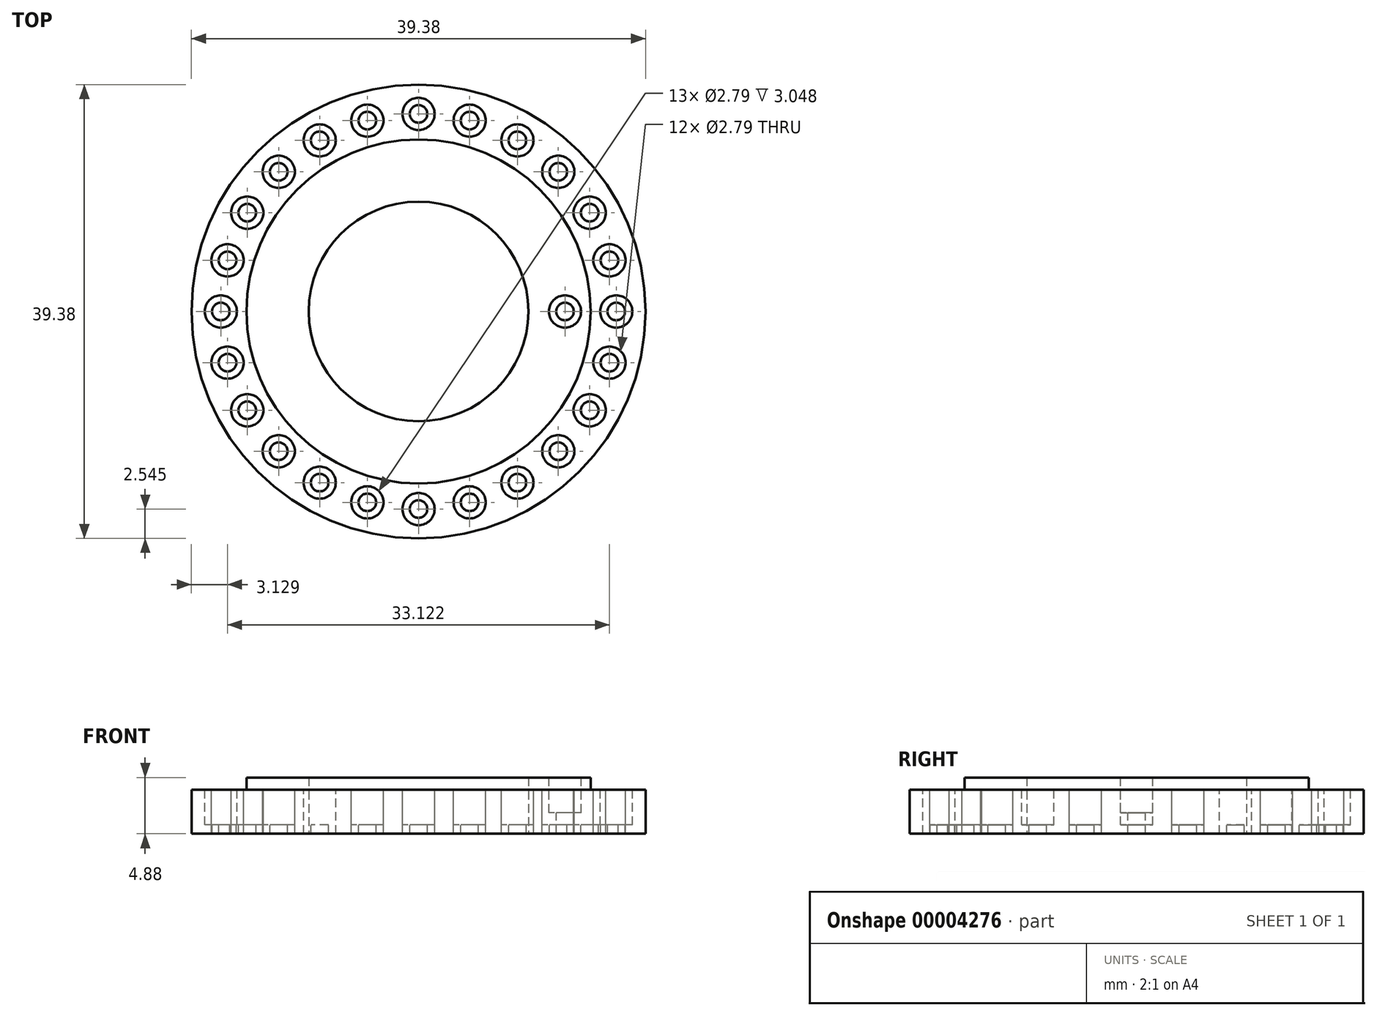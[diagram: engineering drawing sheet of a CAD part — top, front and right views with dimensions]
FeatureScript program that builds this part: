
annotation { "Feature Type Name" : "Feature", "Feature Type Description" : "" }
export const myFeature = defineFeature(function(context is Context, id is Id, definition is map)
    precondition{}
    {
        {
            var Q0;
            Q0=qCreatedBy(makeId("Top.planeOp"),FACE);
            var sketch = newSketch(context, id + "F0", { "sketchPlane" : qUnion([Q0])});
            skCircle(sketch, "E0", {"center": v(0, 0) * mm, "radius": 19.69 * mm});
            skCircle(sketch, "E1", {"center": v(0, 0) * mm, "radius": 14.92 * mm});
            skCircle(sketch, "E2", {"center": v(0, 0) * mm, "radius": 9.53 * mm});
            skSolve(sketch);
        }
        {
            var Q0;
            Q0=makeQuery(id+"F0.imprint","IMPRINT",FACE,{"disambiguationData":[TD([[makeQuery(id+"F0.imprint","IMPRINT",EDGE,{"derivedFrom":sQuery(id+"F0.wireOp",EDGE,"E1")}),1.0]])]});
            extrude(context, id + "F1", {"entities" : qUnion([Q0]), "flatOperationType" : FlatOperationType.REMOVE, "depth" : 4.88 * mm, "offsetDistance" : 25.4 * mm, "domain" : OperationDomain.MODEL});
        }
        {
            var Q0;
            Q0=makeQuery(id+"F0.imprint","IMPRINT",FACE,{"disambiguationData":[TD([[makeQuery(id+"F0.imprint","IMPRINT",EDGE,{"derivedFrom":sQuery(id+"F0.wireOp",EDGE,"E0")}),1.0]])]});
            extrude(context, id + "F2", {"entities" : qUnion([Q0]), "operationType" : NewBodyOperationType.ADD, "flatOperationType" : FlatOperationType.REMOVE, "depth" : 3.8 * mm, "offsetDistance" : 25.4 * mm, "domain" : OperationDomain.MODEL});
        }
        {
            var Q0;
            Q0=makeQuery(id+"F1.opExtrude","CAP_FACE",FACE,{"disambiguationData":[OSD([sQuery(id+"F0.wireOp",EDGE,"E1"),sQuery(id+"F0.wireOp",EDGE,"E2")])],"isStart":false});
            var sketch = newSketch(context, id + "F3", { "sketchPlane" : qUnion([Q0])});
            skLineSegment(sketch, "E3", {"start": v(0, 0) * mm, "end": v(11.3, 0) * mm});
            skCircle(sketch, "E4", {"center": v(12.7, 0) * mm, "radius": 0.76 * mm});
            skLineSegment(sketch, "E5.trimOffspring", {"start": v(14.1, 0) * mm, "end": v(14.92, 0) * mm});
            skCircle(sketch, "E6", {"center": v(12.7, 0) * mm, "radius": 1.4 * mm});
            skSolve(sketch);
        }
        {
            var Q0;
            {var subQ0=sQuery(id+"F3.wireOp",EDGE,"E4");var subQ2=makeQuery(id+"F3.imprint","INTERSECT",VERTEX,{"derivedFrom":[sQuery(id+"F3.wireOp",EDGE,"E3"),subQ0]});Q0=makeQuery(id+"F3.imprint","IMPRINT",FACE,{"disambiguationData":[TD([[makeQuery(id+"F3.imprint","IMPRINT",EDGE,{"disambiguationData":[TD([[subQ2,1.0]])],"derivedFrom":subQ0}),1.0]])]});}
            var Q1;
            Q1=qSketchRegion(id+"F5",true);
            extrude(context, id + "F4", {"entities" : qUnion([Q0, Q1]), "operationType" : NewBodyOperationType.REMOVE, "flatOperationType" : FlatOperationType.REMOVE, "endBound" : BoundingType.THROUGH_ALL, "oppositeDirection" : true, "depth" : 4.44 * mm, "offsetDistance" : 25.4 * mm, "domain" : OperationDomain.MODEL});
        }
        {
            var Q0;
            Q0=makeQuery(id+"F2.opExtrude","CAP_FACE",FACE,{"disambiguationData":[OSD([sQuery(id+"F0.wireOp",EDGE,"E0"),sQuery(id+"F0.wireOp",EDGE,"E1")])],"isStart":false});
            var sketch = newSketch(context, id + "F5", { "sketchPlane" : qUnion([Q0])});
            skLineSegment(sketch, "E7", {"start": v(0, 0) * mm, "end": v(16.38, 0) * mm, "construction": true});
            skLineSegment(sketch, "E8", {"start": v(0, 0) * mm, "end": v(15.82, 4.24) * mm, "construction": true});
            skCircle(sketch, "E9", {"center": v(17.15, 0) * mm, "radius": 0.76 * mm});
            skCircle(sketch, "E10", {"center": v(16.56, 4.44) * mm, "radius": 0.76 * mm});
            skCircle(sketch, "E11.0.MirrorC", {"center": v(14.85, 8.57) * mm, "radius": 0.76 * mm});
            skLineSegment(sketch, "E12", {"start": v(0, 0) * mm, "end": v(14.19, 8.2) * mm, "construction": true});
            skCircle(sketch, "E13.0.MirrorC", {"center": v(12.12, 12.12) * mm, "radius": 0.76 * mm});
            skCircle(sketch, "E14.0.MirrorC", {"center": v(8.57, 14.85) * mm, "radius": 0.76 * mm});
            skLineSegment(sketch, "E15", {"start": v(0, 0) * mm, "end": v(8.2, 14.19) * mm, "construction": true});
            skCircle(sketch, "E16.0.MirrorC", {"center": v(4.44, 16.56) * mm, "radius": 0.76 * mm});
            skCircle(sketch, "E17.0.MirrorC", {"center": v(0, 17.15) * mm, "radius": 0.76 * mm});
            skCircle(sketch, "E18.0.MirrorC", {"center": v(-4.44, 16.56) * mm, "radius": 0.76 * mm});
            skCircle(sketch, "E19.0.MirrorC", {"center": v(-8.57, 14.85) * mm, "radius": 0.76 * mm});
            skLineSegment(sketch, "E20", {"start": v(0, 0) * mm, "end": v(-8.2, 14.19) * mm, "construction": true});
            skCircle(sketch, "E21.0.MirrorC", {"center": v(-12.12, 12.12) * mm, "radius": 0.76 * mm});
            skCircle(sketch, "E22.0.MirrorC", {"center": v(-14.85, 8.57) * mm, "radius": 0.76 * mm});
            skCircle(sketch, "E23.0.MirrorC", {"center": v(-16.56, 4.44) * mm, "radius": 0.76 * mm});
            skCircle(sketch, "E24.0.MirrorC", {"center": v(-17.15, 0) * mm, "radius": 0.76 * mm});
            skCircle(sketch, "E25.0.MirrorC", {"center": v(-16.56, -4.44) * mm, "radius": 0.76 * mm});
            skCircle(sketch, "E26.0.MirrorC", {"center": v(-14.85, -8.57) * mm, "radius": 0.76 * mm});
            skCircle(sketch, "E27.0.MirrorC", {"center": v(-12.12, -12.12) * mm, "radius": 0.76 * mm});
            skCircle(sketch, "E28.0.MirrorC", {"center": v(-8.57, -14.85) * mm, "radius": 0.76 * mm});
            skCircle(sketch, "E29.0.MirrorC", {"center": v(16.56, -4.44) * mm, "radius": 0.76 * mm});
            skCircle(sketch, "E30.0.MirrorC", {"center": v(14.85, -8.57) * mm, "radius": 0.76 * mm});
            skCircle(sketch, "E31.0.MirrorC", {"center": v(12.12, -12.12) * mm, "radius": 0.76 * mm});
            skCircle(sketch, "E32.0.MirrorC", {"center": v(8.57, -14.85) * mm, "radius": 0.76 * mm});
            skCircle(sketch, "E33.0.MirrorC", {"center": v(4.44, -16.56) * mm, "radius": 0.76 * mm});
            skCircle(sketch, "E34.0.MirrorC", {"center": v(0, -17.15) * mm, "radius": 0.76 * mm});
            skCircle(sketch, "E35.0.MirrorC", {"center": v(-4.44, -16.56) * mm, "radius": 0.76 * mm});
            skLineSegment(sketch, "E36.trimOffspring", {"start": v(17.3, 4.63) * mm, "end": v(19.01, 5.1) * mm, "construction": true});
            skLineSegment(sketch, "E37.trimOffspring", {"start": v(17.9, 0) * mm, "end": v(19.69, 0) * mm, "construction": true});
            skCircle(sketch, "E38", {"center": v(17.15, 0) * mm, "radius": 1.4 * mm});
            skCircle(sketch, "E39", {"center": v(16.56, 4.44) * mm, "radius": 1.4 * mm});
            skCircle(sketch, "E40", {"center": v(14.85, 8.57) * mm, "radius": 1.4 * mm});
            skCircle(sketch, "E41", {"center": v(12.12, 12.12) * mm, "radius": 1.4 * mm});
            skCircle(sketch, "E42", {"center": v(8.57, 14.85) * mm, "radius": 1.4 * mm});
            skCircle(sketch, "E43", {"center": v(4.44, 16.56) * mm, "radius": 1.4 * mm});
            skCircle(sketch, "E44", {"center": v(0, 17.15) * mm, "radius": 1.4 * mm});
            skCircle(sketch, "E45", {"center": v(-4.44, 16.56) * mm, "radius": 1.4 * mm});
            skCircle(sketch, "E46", {"center": v(-8.57, 14.85) * mm, "radius": 1.4 * mm});
            skCircle(sketch, "E47", {"center": v(-12.12, 12.12) * mm, "radius": 1.4 * mm});
            skCircle(sketch, "E48", {"center": v(-14.85, 8.57) * mm, "radius": 1.4 * mm});
            skCircle(sketch, "E49", {"center": v(-16.56, 4.44) * mm, "radius": 1.4 * mm});
            skCircle(sketch, "E50", {"center": v(-17.15, 0) * mm, "radius": 1.4 * mm});
            skCircle(sketch, "E51", {"center": v(-16.56, -4.44) * mm, "radius": 1.4 * mm});
            skCircle(sketch, "E52", {"center": v(-14.85, -8.57) * mm, "radius": 1.4 * mm});
            skCircle(sketch, "E53", {"center": v(-12.12, -12.12) * mm, "radius": 1.4 * mm});
            skCircle(sketch, "E54", {"center": v(-8.57, -14.85) * mm, "radius": 1.4 * mm});
            skCircle(sketch, "E55", {"center": v(-4.44, -16.56) * mm, "radius": 1.4 * mm});
            skCircle(sketch, "E56", {"center": v(0, -17.15) * mm, "radius": 1.4 * mm});
            skCircle(sketch, "E57", {"center": v(4.44, -16.56) * mm, "radius": 1.4 * mm});
            skCircle(sketch, "E58", {"center": v(8.57, -14.85) * mm, "radius": 1.4 * mm});
            skCircle(sketch, "E59", {"center": v(12.12, -12.12) * mm, "radius": 1.4 * mm});
            skCircle(sketch, "E60", {"center": v(14.85, -8.57) * mm, "radius": 1.4 * mm});
            skCircle(sketch, "E61", {"center": v(16.56, -4.44) * mm, "radius": 1.4 * mm});
            skSolve(sketch);
        }
        {
            var Q0;
            Q0=makeQuery(id+"F5.imprint","IMPRINT",FACE,{"disambiguationData":[TD([[makeQuery(id+"F5.imprint","IMPRINT",EDGE,{"derivedFrom":sQuery(id+"F5.wireOp",EDGE,"E9")}),1.0]])]});
            var Q1;
            Q1=makeQuery(id+"F5.imprint","IMPRINT",FACE,{"disambiguationData":[TD([[makeQuery(id+"F5.imprint","IMPRINT",EDGE,{"derivedFrom":sQuery(id+"F5.wireOp",EDGE,"E10")}),1.0]])]});
            var Q2;
            Q2=makeQuery(id+"F5.imprint","IMPRINT",FACE,{"disambiguationData":[TD([[makeQuery(id+"F5.imprint","IMPRINT",EDGE,{"derivedFrom":sQuery(id+"F5.wireOp",EDGE,"E11.0.MirrorC")}),-1.0]])]});
            var Q3;
            Q3=makeQuery(id+"F5.imprint","IMPRINT",FACE,{"disambiguationData":[TD([[makeQuery(id+"F5.imprint","IMPRINT",EDGE,{"derivedFrom":sQuery(id+"F5.wireOp",EDGE,"E13.0.MirrorC")}),-1.0]])]});
            var Q4;
            Q4=makeQuery(id+"F5.imprint","IMPRINT",FACE,{"disambiguationData":[TD([[makeQuery(id+"F5.imprint","IMPRINT",EDGE,{"derivedFrom":sQuery(id+"F5.wireOp",EDGE,"E14.0.MirrorC")}),-1.0]])]});
            var Q5;
            Q5=makeQuery(id+"F5.imprint","IMPRINT",FACE,{"disambiguationData":[TD([[makeQuery(id+"F5.imprint","IMPRINT",EDGE,{"derivedFrom":sQuery(id+"F5.wireOp",EDGE,"E16.0.MirrorC")}),1.0]])]});
            var Q6;
            Q6=makeQuery(id+"F5.imprint","IMPRINT",FACE,{"disambiguationData":[TD([[makeQuery(id+"F5.imprint","IMPRINT",EDGE,{"derivedFrom":sQuery(id+"F5.wireOp",EDGE,"E17.0.MirrorC")}),1.0]])]});
            var Q7;
            Q7=makeQuery(id+"F5.imprint","IMPRINT",FACE,{"disambiguationData":[TD([[makeQuery(id+"F5.imprint","IMPRINT",EDGE,{"derivedFrom":sQuery(id+"F5.wireOp",EDGE,"E18.0.MirrorC")}),-1.0]])]});
            var Q8;
            Q8=makeQuery(id+"F5.imprint","IMPRINT",FACE,{"disambiguationData":[TD([[makeQuery(id+"F5.imprint","IMPRINT",EDGE,{"derivedFrom":sQuery(id+"F5.wireOp",EDGE,"E19.0.MirrorC")}),-1.0]])]});
            var Q9;
            Q9=makeQuery(id+"F5.imprint","IMPRINT",FACE,{"disambiguationData":[TD([[makeQuery(id+"F5.imprint","IMPRINT",EDGE,{"derivedFrom":sQuery(id+"F5.wireOp",EDGE,"E21.0.MirrorC")}),1.0]])]});
            var Q10;
            Q10=makeQuery(id+"F5.imprint","IMPRINT",FACE,{"disambiguationData":[TD([[makeQuery(id+"F5.imprint","IMPRINT",EDGE,{"derivedFrom":sQuery(id+"F5.wireOp",EDGE,"E22.0.MirrorC")}),-1.0]])]});
            var Q11;
            Q11=makeQuery(id+"F5.imprint","IMPRINT",FACE,{"disambiguationData":[TD([[makeQuery(id+"F5.imprint","IMPRINT",EDGE,{"derivedFrom":sQuery(id+"F5.wireOp",EDGE,"E23.0.MirrorC")}),-1.0]])]});
            var Q12;
            Q12=makeQuery(id+"F5.imprint","IMPRINT",FACE,{"disambiguationData":[TD([[makeQuery(id+"F5.imprint","IMPRINT",EDGE,{"derivedFrom":sQuery(id+"F5.wireOp",EDGE,"E24.0.MirrorC")}),1.0]])]});
            var Q13;
            Q13=makeQuery(id+"F5.imprint","IMPRINT",FACE,{"disambiguationData":[TD([[makeQuery(id+"F5.imprint","IMPRINT",EDGE,{"derivedFrom":sQuery(id+"F5.wireOp",EDGE,"E25.0.MirrorC")}),1.0]])]});
            var Q14;
            Q14=makeQuery(id+"F5.imprint","IMPRINT",FACE,{"disambiguationData":[TD([[makeQuery(id+"F5.imprint","IMPRINT",EDGE,{"derivedFrom":sQuery(id+"F5.wireOp",EDGE,"E26.0.MirrorC")}),1.0]])]});
            var Q15;
            Q15=makeQuery(id+"F5.imprint","IMPRINT",FACE,{"disambiguationData":[TD([[makeQuery(id+"F5.imprint","IMPRINT",EDGE,{"derivedFrom":sQuery(id+"F5.wireOp",EDGE,"E27.0.MirrorC")}),-1.0]])]});
            var Q16;
            Q16=makeQuery(id+"F5.imprint","IMPRINT",FACE,{"disambiguationData":[TD([[makeQuery(id+"F5.imprint","IMPRINT",EDGE,{"derivedFrom":sQuery(id+"F5.wireOp",EDGE,"E28.0.MirrorC")}),-1.0]])]});
            var Q17;
            Q17=makeQuery(id+"F5.imprint","IMPRINT",FACE,{"disambiguationData":[TD([[makeQuery(id+"F5.imprint","IMPRINT",EDGE,{"derivedFrom":sQuery(id+"F5.wireOp",EDGE,"E35.0.MirrorC")}),1.0]])]});
            var Q18;
            Q18=makeQuery(id+"F5.imprint","IMPRINT",FACE,{"disambiguationData":[TD([[makeQuery(id+"F5.imprint","IMPRINT",EDGE,{"derivedFrom":sQuery(id+"F5.wireOp",EDGE,"E34.0.MirrorC")}),-1.0]])]});
            var Q19;
            Q19=makeQuery(id+"F5.imprint","IMPRINT",FACE,{"disambiguationData":[TD([[makeQuery(id+"F5.imprint","IMPRINT",EDGE,{"derivedFrom":sQuery(id+"F5.wireOp",EDGE,"E33.0.MirrorC")}),-1.0]])]});
            var Q20;
            Q20=makeQuery(id+"F5.imprint","IMPRINT",FACE,{"disambiguationData":[TD([[makeQuery(id+"F5.imprint","IMPRINT",EDGE,{"derivedFrom":sQuery(id+"F5.wireOp",EDGE,"E32.0.MirrorC")}),1.0]])]});
            var Q21;
            Q21=makeQuery(id+"F5.imprint","IMPRINT",FACE,{"disambiguationData":[TD([[makeQuery(id+"F5.imprint","IMPRINT",EDGE,{"derivedFrom":sQuery(id+"F5.wireOp",EDGE,"E31.0.MirrorC")}),1.0]])]});
            var Q22;
            Q22=makeQuery(id+"F5.imprint","IMPRINT",FACE,{"disambiguationData":[TD([[makeQuery(id+"F5.imprint","IMPRINT",EDGE,{"derivedFrom":sQuery(id+"F5.wireOp",EDGE,"E30.0.MirrorC")}),1.0]])]});
            var Q23;
            Q23=makeQuery(id+"F5.imprint","IMPRINT",FACE,{"disambiguationData":[TD([[makeQuery(id+"F5.imprint","IMPRINT",EDGE,{"derivedFrom":sQuery(id+"F5.wireOp",EDGE,"E29.0.MirrorC")}),-1.0]])]});
            extrude(context, id + "F6", {"entities" : qUnion([Q0, Q1, Q2, Q3, Q4, Q5, Q6, Q7, Q8, Q9, Q10, Q11, Q12, Q13, Q14, Q15, Q16, Q17, Q18, Q19, Q20, Q21, Q22, Q23]), "operationType" : NewBodyOperationType.REMOVE, "flatOperationType" : FlatOperationType.REMOVE, "endBound" : BoundingType.THROUGH_ALL, "oppositeDirection" : true, "depth" : 4.44 * mm, "offsetDistance" : 25.4 * mm, "domain" : OperationDomain.MODEL});
        }
        {
            var Q0;
            Q0=qSketchRegion(id+"F3",true);
            extrude(context, id + "F7", {"entities" : qUnion([Q0]), "operationType" : NewBodyOperationType.REMOVE, "flatOperationType" : FlatOperationType.REMOVE, "oppositeDirection" : true, "depth" : 3.05 * mm, "offsetDistance" : 25.4 * mm, "domain" : OperationDomain.MODEL});
        }
        {
            var Q0;
            Q0=makeQuery(id+"F5.imprint","IMPRINT",FACE,{"disambiguationData":[TD([[makeQuery(id+"F5.imprint","IMPRINT",EDGE,{"derivedFrom":sQuery(id+"F5.wireOp",EDGE,"E9")}),-1.0]])]});
            var Q1;
            Q1=makeQuery(id+"F5.imprint","IMPRINT",FACE,{"disambiguationData":[TD([[makeQuery(id+"F5.imprint","IMPRINT",EDGE,{"derivedFrom":sQuery(id+"F5.wireOp",EDGE,"E10")}),-1.0]])]});
            var Q2;
            Q2=makeQuery(id+"F5.imprint","IMPRINT",FACE,{"disambiguationData":[TD([[makeQuery(id+"F5.imprint","IMPRINT",EDGE,{"derivedFrom":sQuery(id+"F5.wireOp",EDGE,"E29.0.MirrorC")}),1.0]])]});
            var Q3;
            Q3=makeQuery(id+"F5.imprint","IMPRINT",FACE,{"disambiguationData":[TD([[makeQuery(id+"F5.imprint","IMPRINT",EDGE,{"derivedFrom":sQuery(id+"F5.wireOp",EDGE,"E11.0.MirrorC")}),1.0]])]});
            var Q4;
            Q4=makeQuery(id+"F5.imprint","IMPRINT",FACE,{"disambiguationData":[TD([[makeQuery(id+"F5.imprint","IMPRINT",EDGE,{"derivedFrom":sQuery(id+"F5.wireOp",EDGE,"E13.0.MirrorC")}),1.0]])]});
            var Q5;
            Q5=makeQuery(id+"F5.imprint","IMPRINT",FACE,{"disambiguationData":[TD([[makeQuery(id+"F5.imprint","IMPRINT",EDGE,{"derivedFrom":sQuery(id+"F5.wireOp",EDGE,"E14.0.MirrorC")}),1.0]])]});
            var Q6;
            Q6=makeQuery(id+"F5.imprint","IMPRINT",FACE,{"disambiguationData":[TD([[makeQuery(id+"F5.imprint","IMPRINT",EDGE,{"derivedFrom":sQuery(id+"F5.wireOp",EDGE,"E16.0.MirrorC")}),-1.0]])]});
            var Q7;
            Q7=makeQuery(id+"F5.imprint","IMPRINT",FACE,{"disambiguationData":[TD([[makeQuery(id+"F5.imprint","IMPRINT",EDGE,{"derivedFrom":sQuery(id+"F5.wireOp",EDGE,"E17.0.MirrorC")}),-1.0]])]});
            var Q8;
            Q8=makeQuery(id+"F5.imprint","IMPRINT",FACE,{"disambiguationData":[TD([[makeQuery(id+"F5.imprint","IMPRINT",EDGE,{"derivedFrom":sQuery(id+"F5.wireOp",EDGE,"E18.0.MirrorC")}),1.0]])]});
            var Q9;
            Q9=makeQuery(id+"F5.imprint","IMPRINT",FACE,{"disambiguationData":[TD([[makeQuery(id+"F5.imprint","IMPRINT",EDGE,{"derivedFrom":sQuery(id+"F5.wireOp",EDGE,"E19.0.MirrorC")}),1.0]])]});
            var Q10;
            Q10=makeQuery(id+"F5.imprint","IMPRINT",FACE,{"disambiguationData":[TD([[makeQuery(id+"F5.imprint","IMPRINT",EDGE,{"derivedFrom":sQuery(id+"F5.wireOp",EDGE,"E21.0.MirrorC")}),-1.0]])]});
            var Q11;
            Q11=makeQuery(id+"F5.imprint","IMPRINT",FACE,{"disambiguationData":[TD([[makeQuery(id+"F5.imprint","IMPRINT",EDGE,{"derivedFrom":sQuery(id+"F5.wireOp",EDGE,"E22.0.MirrorC")}),1.0]])]});
            var Q12;
            Q12=makeQuery(id+"F5.imprint","IMPRINT",FACE,{"disambiguationData":[TD([[makeQuery(id+"F5.imprint","IMPRINT",EDGE,{"derivedFrom":sQuery(id+"F5.wireOp",EDGE,"E23.0.MirrorC")}),1.0]])]});
            var Q13;
            Q13=makeQuery(id+"F5.imprint","IMPRINT",FACE,{"disambiguationData":[TD([[makeQuery(id+"F5.imprint","IMPRINT",EDGE,{"derivedFrom":sQuery(id+"F5.wireOp",EDGE,"E24.0.MirrorC")}),-1.0]])]});
            var Q14;
            Q14=makeQuery(id+"F5.imprint","IMPRINT",FACE,{"disambiguationData":[TD([[makeQuery(id+"F5.imprint","IMPRINT",EDGE,{"derivedFrom":sQuery(id+"F5.wireOp",EDGE,"E25.0.MirrorC")}),-1.0]])]});
            var Q15;
            Q15=makeQuery(id+"F5.imprint","IMPRINT",FACE,{"disambiguationData":[TD([[makeQuery(id+"F5.imprint","IMPRINT",EDGE,{"derivedFrom":sQuery(id+"F5.wireOp",EDGE,"E26.0.MirrorC")}),-1.0]])]});
            var Q16;
            Q16=makeQuery(id+"F5.imprint","IMPRINT",FACE,{"disambiguationData":[TD([[makeQuery(id+"F5.imprint","IMPRINT",EDGE,{"derivedFrom":sQuery(id+"F5.wireOp",EDGE,"E27.0.MirrorC")}),1.0]])]});
            var Q17;
            Q17=makeQuery(id+"F5.imprint","IMPRINT",FACE,{"disambiguationData":[TD([[makeQuery(id+"F5.imprint","IMPRINT",EDGE,{"derivedFrom":sQuery(id+"F5.wireOp",EDGE,"E28.0.MirrorC")}),1.0]])]});
            var Q18;
            Q18=makeQuery(id+"F5.imprint","IMPRINT",FACE,{"disambiguationData":[TD([[makeQuery(id+"F5.imprint","IMPRINT",EDGE,{"derivedFrom":sQuery(id+"F5.wireOp",EDGE,"E35.0.MirrorC")}),-1.0]])]});
            var Q19;
            Q19=makeQuery(id+"F5.imprint","IMPRINT",FACE,{"disambiguationData":[TD([[makeQuery(id+"F5.imprint","IMPRINT",EDGE,{"derivedFrom":sQuery(id+"F5.wireOp",EDGE,"E34.0.MirrorC")}),1.0]])]});
            var Q20;
            Q20=makeQuery(id+"F5.imprint","IMPRINT",FACE,{"disambiguationData":[TD([[makeQuery(id+"F5.imprint","IMPRINT",EDGE,{"derivedFrom":sQuery(id+"F5.wireOp",EDGE,"E33.0.MirrorC")}),1.0]])]});
            var Q21;
            Q21=makeQuery(id+"F5.imprint","IMPRINT",FACE,{"disambiguationData":[TD([[makeQuery(id+"F5.imprint","IMPRINT",EDGE,{"derivedFrom":sQuery(id+"F5.wireOp",EDGE,"E32.0.MirrorC")}),-1.0]])]});
            var Q22;
            Q22=makeQuery(id+"F5.imprint","IMPRINT",FACE,{"disambiguationData":[TD([[makeQuery(id+"F5.imprint","IMPRINT",EDGE,{"derivedFrom":sQuery(id+"F5.wireOp",EDGE,"E31.0.MirrorC")}),-1.0]])]});
            var Q23;
            Q23=makeQuery(id+"F5.imprint","IMPRINT",FACE,{"disambiguationData":[TD([[makeQuery(id+"F5.imprint","IMPRINT",EDGE,{"derivedFrom":sQuery(id+"F5.wireOp",EDGE,"E30.0.MirrorC")}),-1.0]])]});
            extrude(context, id + "F8", {"entities" : qUnion([Q0, Q1, Q2, Q3, Q4, Q5, Q6, Q7, Q8, Q9, Q10, Q11, Q12, Q13, Q14, Q15, Q16, Q17, Q18, Q19, Q20, Q21, Q22, Q23]), "operationType" : NewBodyOperationType.REMOVE, "flatOperationType" : FlatOperationType.REMOVE, "oppositeDirection" : true, "depth" : 3.05 * mm, "offsetDistance" : 25.4 * mm, "domain" : OperationDomain.MODEL});
        }
    });
